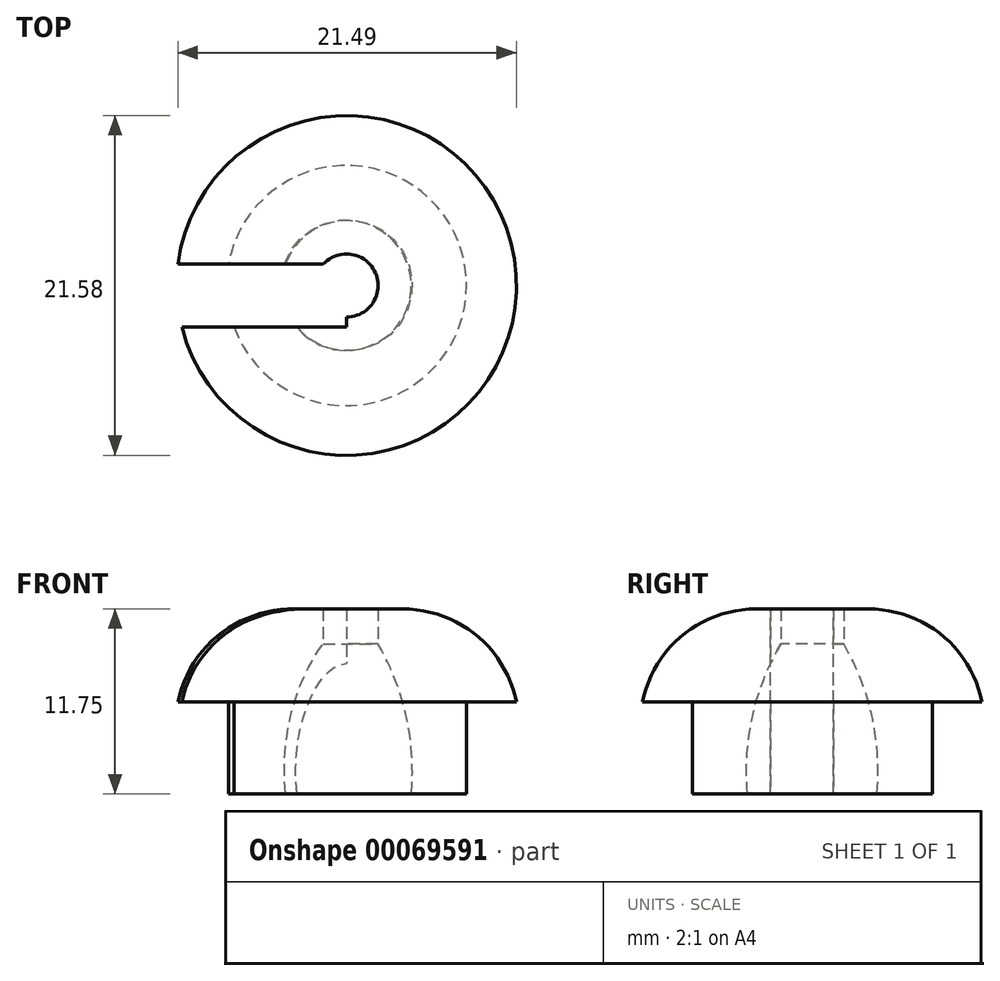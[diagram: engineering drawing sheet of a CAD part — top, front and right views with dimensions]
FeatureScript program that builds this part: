
annotation { "Feature Type Name" : "Feature", "Feature Type Description" : "" }
export const myFeature = defineFeature(function(context is Context, id is Id, definition is map)
    precondition{}
    {
        {
            var Q0;
            Q0=qCreatedBy(makeId("Top.planeOp"),FACE);
            var sketch = newSketch(context, id + "F0", { "sketchPlane" : qUnion([Q0])});
            skCircle(sketch, "E0", {"center": v(0, 0) * mm, "radius": 7.63 * mm});
            skSolve(sketch);
        }
        {
            var Q0;
            Q0=qCreatedBy(makeId("Front.planeOp"),FACE);
            var sketch = newSketch(context, id + "F1", { "sketchPlane" : qUnion([Q0])});
            skLineSegment(sketch, "E1.0", {"start": v(-7.63, 0) * mm, "end": v(7.63, 0) * mm});
            skLineSegment(sketch, "E2", {"start": v(7.63, 0) * mm, "end": v(7.63, 5.83) * mm});
            skLineSegment(sketch, "E3", {"start": v(7.63, 5.83) * mm, "end": v(10.79, 5.83) * mm});
            skLineSegment(sketch, "E4", {"start": v(7.63, 5.83) * mm, "end": v(7.63, 9.79) * mm, "construction": true});
            skLineSegment(sketch, "E5", {"start": v(6.43, 0) * mm, "end": v(6.42, 8.96) * mm});
            skLineSegment(sketch, "E6", {"start": v(0, 0) * mm, "end": v(0, 10.94) * mm, "construction": true});
            skLineSegment(sketch, "E7", {"start": v(0, 10.94) * mm, "end": v(0, 16.33) * mm, "construction": true});
            skLineSegment(sketch, "E8", {"start": v(2, 0) * mm, "end": v(2, 16.21) * mm, "construction": true});
            skLineSegment(sketch, "E9", {"start": v(2, 11.75) * mm, "end": v(2, 9.52) * mm});
            skArc(sketch, "E10", {"start": v(4.11, 0) * mm, "mid": v(3.8, 4.92) * mm, "end": v(2, 9.52) * mm});
            skLineSegment(sketch, "E11", {"start": v(2, 11.75) * mm, "end": v(3.57, 11.75) * mm});
            skArc(sketch, "E12", {"start": v(10.79, 5.83) * mm, "mid": v(8.24, 10.08) * mm, "end": v(3.57, 11.75) * mm});
            skSolve(sketch);
        }
        {
            var Q0;
            {var subQ0=sQuery(id+"F1.wireOp",EDGE,"E2");Q0=makeQuery(id+"F1.imprint","IMPRINT",FACE,{"disambiguationData":[TD([[makeQuery(id+"F1.imprint","IMPRINT",EDGE,{"derivedFrom":subQ0}),1.0]])]});}
            var Q1;
            Q1=sQuery(id+"F0.wireOp",EDGE,"E0");
            revolve(context, id + "F2", {"entities" : qUnion([Q0]), "axis" : qUnion([Q1]), "revolveType" : RevolveType.FULL});
        }
        {
            var Q0;
            Q0=qCreatedBy(makeId("Right.planeOp"),FACE);
            var sketch = newSketch(context, id + "F3", { "sketchPlane" : qUnion([Q0])});
            skLineSegment(sketch, "E13.bottom", {"start": v(1.35, 11.97) * mm, "end": v(-2.65, 11.97) * mm});
            skLineSegment(sketch, "E13.top", {"start": v(1.35, -1.2) * mm, "end": v(-2.65, -1.2) * mm});
            skLineSegment(sketch, "E13.left", {"start": v(1.35, 11.97) * mm, "end": v(1.35, -1.2) * mm});
            skLineSegment(sketch, "E13.right", {"start": v(-2.65, 11.97) * mm, "end": v(-2.65, -1.2) * mm});
            skSolve(sketch);
        }
        {
            var Q0;
            Q0=makeQuery(id+"F3.imprint","IMPRINT",FACE,{"disambiguationData":[TD([[makeQuery(id+"F3.imprint","IMPRINT",EDGE,{"derivedFrom":sQuery(id+"F3.wireOp",EDGE,"E13.bottom")}),1.0]])]});
            extrude(context, id + "F4", {"entities" : qUnion([Q0]), "operationType" : NewBodyOperationType.REMOVE, "endBound" : BoundingType.THROUGH_ALL, "oppositeDirection" : true, "depth" : 25 * mm});
        }
    });
